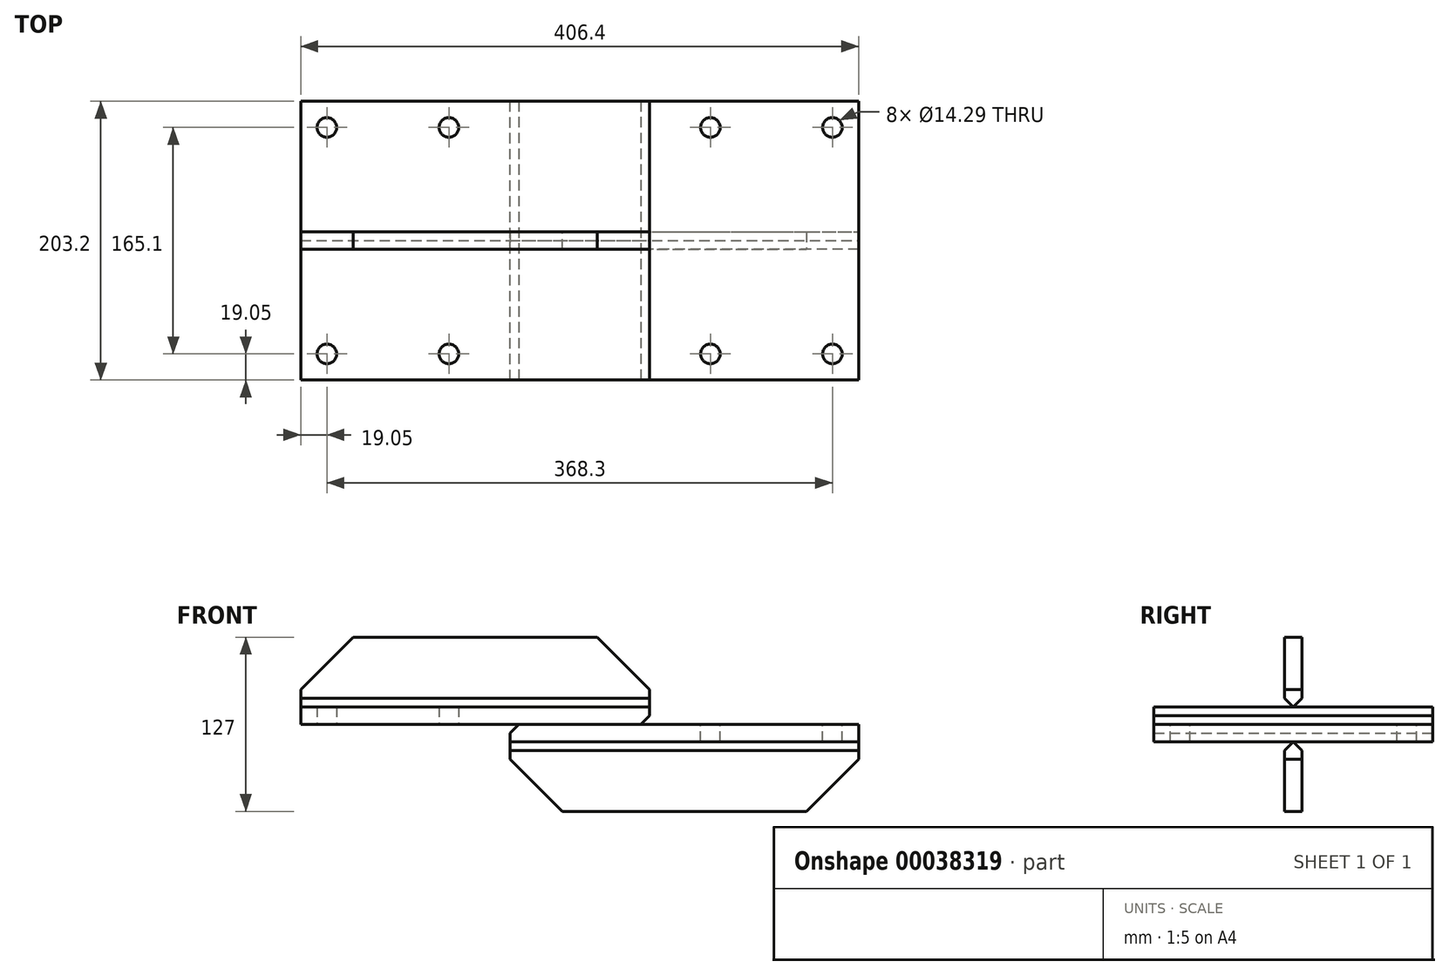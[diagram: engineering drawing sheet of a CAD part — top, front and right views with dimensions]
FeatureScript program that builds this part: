
annotation { "Feature Type Name" : "Feature", "Feature Type Description" : "" }
export const myFeature = defineFeature(function(context is Context, id is Id, definition is map)
    precondition{}
    {
        {
            var Q0;
            Q0=qCreatedBy(makeId("Top.planeOp"),FACE);
            var sketch = newSketch(context, id + "F0", { "sketchPlane" : qUnion([Q0])});
            skLineSegment(sketch, "E0", {"start": v(0, 106.75) * mm, "end": v(0, -105.6) * mm, "construction": true});
            skLineSegment(sketch, "E1.0", {"start": v(-203.2, 106.75) * mm, "end": v(-203.2, -105.6) * mm, "construction": true});
            skLineSegment(sketch, "E2.MirrorCS", {"start": v(203.2, 106.75) * mm, "end": v(203.2, -105.6) * mm, "construction": true});
            skLineSegment(sketch, "E3", {"start": v(-283.64, 0) * mm, "end": v(308.6, 0) * mm, "construction": true});
            skLineSegment(sketch, "E4.0", {"start": v(-283.64, -101.6) * mm, "end": v(308.6, -101.6) * mm, "construction": true});
            skLineSegment(sketch, "E5.bottom", {"start": v(-203.2, -101.6) * mm, "end": v(50.8, -101.6) * mm});
            skLineSegment(sketch, "E5.top", {"start": v(-203.2, 101.6) * mm, "end": v(50.8, 101.6) * mm});
            skLineSegment(sketch, "E5.left", {"start": v(-203.2, -101.6) * mm, "end": v(-203.2, 101.6) * mm});
            skLineSegment(sketch, "E5.right", {"start": v(50.8, -101.6) * mm, "end": v(50.8, 101.6) * mm});
            skLineSegment(sketch, "E6.0", {"start": v(-139.7, -101.6) * mm, "end": v(-139.7, 101.6) * mm, "construction": true});
            skLineSegment(sketch, "E7.0", {"start": v(-184.15, -101.6) * mm, "end": v(-184.15, 101.6) * mm, "construction": true});
            skLineSegment(sketch, "E8.0", {"start": v(-283.64, -82.55) * mm, "end": v(308.6, -82.55) * mm, "construction": true});
            skCircle(sketch, "E9", {"center": v(-184.15, -82.55) * mm, "radius": 7.14 * mm});
            skCircle(sketch, "E10.MirrorC", {"center": v(-95.25, -82.55) * mm, "radius": 7.14 * mm});
            skCircle(sketch, "E11.MirrorC", {"center": v(-95.25, 82.55) * mm, "radius": 7.14 * mm});
            skCircle(sketch, "E12.MirrorC", {"center": v(-184.15, 82.55) * mm, "radius": 7.14 * mm});
            skSolve(sketch);
        }
        {
            var Q0;
            Q0=makeQuery(id+"F0.imprint","IMPRINT",FACE,{"disambiguationData":[TD([[makeQuery(id+"F0.imprint","IMPRINT",EDGE,{"derivedFrom":sQuery(id+"F0.wireOp",EDGE,"E5.bottom")}),1.0]])]});
            extrude(context, id + "F1", {"entities" : qUnion([Q0]), "depth" : 12.7 * mm});
        }
        {
            var Q0;
            Q0=makeQuery(id+"F1.opExtrude","CAP_FACE",FACE,{"disambiguationData":[OSD([sQuery(id+"F0.wireOp",EDGE,"E5.bottom"),sQuery(id+"F0.wireOp",EDGE,"E5.top"),sQuery(id+"F0.wireOp",EDGE,"E5.left"),sQuery(id+"F0.wireOp",EDGE,"E5.right"),sQuery(id+"F0.wireOp",EDGE,"E9"),sQuery(id+"F0.wireOp",EDGE,"E10.MirrorC"),sQuery(id+"F0.wireOp",EDGE,"E11.MirrorC"),sQuery(id+"F0.wireOp",EDGE,"E12.MirrorC")])],"isStart":true});
            var sketch = newSketch(context, id + "F2", { "sketchPlane" : qUnion([Q0])});
            skLineSegment(sketch, "E13.0", {"start": v(-283.64, 101.6) * mm, "end": v(308.6, 101.6) * mm, "construction": true});
            skLineSegment(sketch, "E14.0", {"start": v(203.2, -106.75) * mm, "end": v(203.2, 105.6) * mm, "construction": true});
            skLineSegment(sketch, "E15.bottom", {"start": v(203.2, 101.6) * mm, "end": v(-50.8, 101.6) * mm});
            skLineSegment(sketch, "E15.top", {"start": v(203.2, -101.6) * mm, "end": v(-50.8, -101.6) * mm});
            skLineSegment(sketch, "E15.left", {"start": v(203.2, 101.6) * mm, "end": v(203.2, -101.6) * mm});
            skLineSegment(sketch, "E15.right", {"start": v(-50.8, 101.6) * mm, "end": v(-50.8, -101.6) * mm});
            skLineSegment(sketch, "E16.0", {"start": v(139.7, 101.6) * mm, "end": v(139.7, -101.6) * mm, "construction": true});
            skLineSegment(sketch, "E17.0", {"start": v(184.15, 101.6) * mm, "end": v(184.15, -101.6) * mm, "construction": true});
            skLineSegment(sketch, "E18.0", {"start": v(-283.64, 82.55) * mm, "end": v(308.6, 82.55) * mm, "construction": true});
            skCircle(sketch, "E19", {"center": v(184.15, 82.55) * mm, "radius": 7.14 * mm});
            skCircle(sketch, "E20.MirrorC", {"center": v(95.25, 82.55) * mm, "radius": 7.14 * mm});
            skCircle(sketch, "E21.MirrorC", {"center": v(95.25, -82.55) * mm, "radius": 7.14 * mm});
            skCircle(sketch, "E22.MirrorC", {"center": v(184.15, -82.55) * mm, "radius": 7.14 * mm});
            skSolve(sketch);
        }
        {
            var Q0;
            Q0=qSketchRegion(id+"F2",true);
            extrude(context, id + "F3", {"entities" : qUnion([Q0]), "depth" : 12.7 * mm});
        }
        {
            var Q0;
            Q0=makeQuery(id+"F1.opExtrude","CAP_FACE",FACE,{"disambiguationData":[OSD([sQuery(id+"F0.wireOp",EDGE,"E5.bottom"),sQuery(id+"F0.wireOp",EDGE,"E5.top"),sQuery(id+"F0.wireOp",EDGE,"E5.left"),sQuery(id+"F0.wireOp",EDGE,"E5.right"),sQuery(id+"F0.wireOp",EDGE,"E9"),sQuery(id+"F0.wireOp",EDGE,"E10.MirrorC"),sQuery(id+"F0.wireOp",EDGE,"E11.MirrorC"),sQuery(id+"F0.wireOp",EDGE,"E12.MirrorC")])],"isStart":false});
            var sketch = newSketch(context, id + "F4", { "sketchPlane" : qUnion([Q0])});
            skLineSegment(sketch, "E23.0", {"start": v(-283.64, 0) * mm, "end": v(308.6, 0) * mm, "construction": true});
            skLineSegment(sketch, "E24.0", {"start": v(-203.2, -6.35) * mm, "end": v(50.8, -6.35) * mm});
            skLineSegment(sketch, "E25.0", {"start": v(-203.2, -6.35) * mm, "end": v(-203.2, 6.35) * mm});
            skLineSegment(sketch, "E26.0", {"start": v(50.8, -6.35) * mm, "end": v(50.8, 6.35) * mm});
            skLineSegment(sketch, "E27.MirrorCS", {"start": v(-203.2, 6.35) * mm, "end": v(50.8, 6.35) * mm});
            skPoint(sketch, "E28.orphan", {"position": v(-283.64, 6.35) * mm});
            skPoint(sketch, "E29.orphan", {"position": v(-283.64, -6.35) * mm});
            skPoint(sketch, "E30.orphan", {"position": v(308.6, 6.35) * mm});
            skPoint(sketch, "E31.orphan", {"position": v(308.6, -6.35) * mm});
            skPoint(sketch, "E32.orphan", {"position": v(50.8, 101.6) * mm});
            skPoint(sketch, "E33.orphan", {"position": v(50.8, -101.6) * mm});
            skPoint(sketch, "E34.orphan", {"position": v(-203.2, -101.6) * mm});
            skPoint(sketch, "E35.orphan", {"position": v(-203.2, 101.6) * mm});
            skSolve(sketch);
        }
        {
            var Q0;
            Q0=qSketchRegion(id+"F4",true);
            extrude(context, id + "F5", {"entities" : qUnion([Q0]), "depth" : 50.8 * mm});
        }
        {
            var Q0;
            Q0=makeQuery(id+"F5.opExtrude","CAP_EDGE",EDGE,{"disambiguationData":[OSD([sQuery(id+"F4.wireOp",EDGE,"E25.0")])],"isStart":false});
            var Q1;
            Q1=makeQuery(id+"F5.opExtrude","CAP_EDGE",EDGE,{"disambiguationData":[OSD([sQuery(id+"F4.wireOp",EDGE,"E26.0")])],"isStart":false});
            chamfer(context, id + "F6", {"entities" : qUnion([Q0, Q1]), "width" : 38.1 * mm, "tangentPropagation" : true});
        }
        {
            var Q0;
            Q0=makeQuery(id+"F3.opExtrude","CAP_FACE",FACE,{"disambiguationData":[OSD([sQuery(id+"F2.wireOp",EDGE,"E15.bottom"),sQuery(id+"F2.wireOp",EDGE,"E15.top"),sQuery(id+"F2.wireOp",EDGE,"E15.left"),sQuery(id+"F2.wireOp",EDGE,"E15.right"),sQuery(id+"F2.wireOp",EDGE,"E19"),sQuery(id+"F2.wireOp",EDGE,"E20.MirrorC"),sQuery(id+"F2.wireOp",EDGE,"E21.MirrorC"),sQuery(id+"F2.wireOp",EDGE,"E22.MirrorC")])],"isStart":false});
            var sketch = newSketch(context, id + "F7", { "sketchPlane" : qUnion([Q0])});
            skLineSegment(sketch, "E36.0", {"start": v(-283.64, 0) * mm, "end": v(308.6, 0) * mm, "construction": true});
            skLineSegment(sketch, "E37.0", {"start": v(-50.8, 101.6) * mm, "end": v(-50.8, -101.6) * mm});
            skLineSegment(sketch, "E38.0", {"start": v(203.2, -106.75) * mm, "end": v(203.2, 105.6) * mm});
            skLineSegment(sketch, "E39.0", {"start": v(-283.64, -6.35) * mm, "end": v(308.6, -6.35) * mm});
            skLineSegment(sketch, "E40.MirrorCS", {"start": v(-283.64, 6.35) * mm, "end": v(308.6, 6.35) * mm});
            skSolve(sketch);
        }
        {
            var Q0;
            {var subQ0=sQuery(id+"F7.wireOp",EDGE,"E40.MirrorCS");var subQ3=sQuery(id+"F7.wireOp",EDGE,"E37.0");var subQ4=makeQuery(id+"F7.imprint","INTERSECT",VERTEX,{"derivedFrom":[subQ3,subQ0]});Q0=makeQuery(id+"F7.imprint","IMPRINT",FACE,{"disambiguationData":[TD([[makeQuery(id+"F7.imprint","IMPRINT",EDGE,{"disambiguationData":[TD([[subQ4,-1.0]])],"derivedFrom":subQ3}),1.0]])]});}
            extrude(context, id + "F8", {"entities" : qUnion([Q0]), "depth" : 50.8 * mm});
        }
        {
            var Q0;
            Q0=makeQuery(id+"F8.opExtrude","CAP_EDGE",EDGE,{"disambiguationData":[OSD([sQuery(id+"F7.wireOp",EDGE,"E38.0")])],"isStart":false});
            var Q1;
            Q1=makeQuery(id+"F8.opExtrude","CAP_EDGE",EDGE,{"disambiguationData":[OSD([sQuery(id+"F7.wireOp",EDGE,"E37.0")])],"isStart":false});
            chamfer(context, id + "F9", {"entities" : qUnion([Q0, Q1]), "width" : 38.1 * mm, "tangentPropagation" : true});
        }
        {
            var Q0;
            Q0=makeQuery(id+"F1.opExtrude","CAP_EDGE",EDGE,{"disambiguationData":[OSD([sQuery(id+"F0.wireOp",EDGE,"E5.right")])],"isStart":true});
            var Q1;
            Q1=makeQuery(id+"F5.opExtrude","CAP_EDGE",EDGE,{"disambiguationData":[OSD([sQuery(id+"F4.wireOp",EDGE,"E24.0")])],"isStart":true});
            var Q2;
            Q2=makeQuery(id+"F5.opExtrude","CAP_EDGE",EDGE,{"disambiguationData":[OSD([sQuery(id+"F4.wireOp",EDGE,"E27.MirrorCS")])],"isStart":true});
            var Q3;
            Q3=makeQuery(id+"F3.opExtrude","CAP_EDGE",EDGE,{"disambiguationData":[OSD([sQuery(id+"F2.wireOp",EDGE,"E15.right")])],"isStart":true});
            var Q4;
            Q4=makeQuery(id+"F8.opExtrude","CAP_EDGE",EDGE,{"disambiguationData":[OSD([sQuery(id+"F7.wireOp",EDGE,"E39.0")])],"isStart":true});
            var Q5;
            Q5=makeQuery(id+"F8.opExtrude","CAP_EDGE",EDGE,{"disambiguationData":[OSD([sQuery(id+"F7.wireOp",EDGE,"E40.MirrorCS")])],"isStart":true});
            chamfer(context, id + "F10", {"entities" : qUnion([Q0, Q1, Q2, Q3, Q4, Q5]), "width" : 6.35 * mm, "tangentPropagation" : true});
        }
    });
